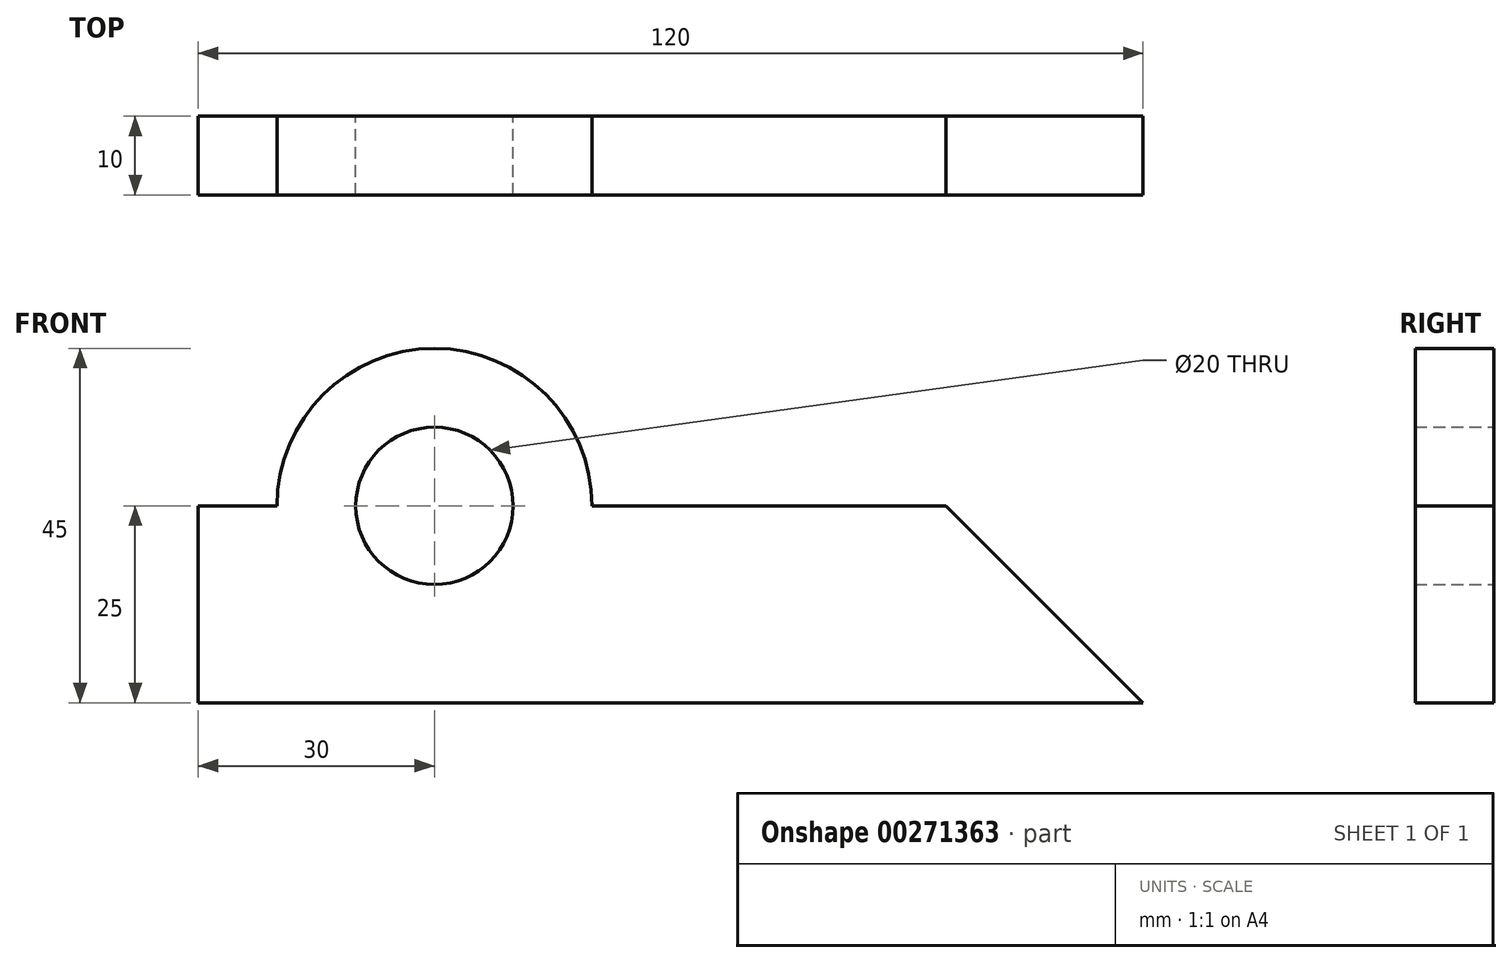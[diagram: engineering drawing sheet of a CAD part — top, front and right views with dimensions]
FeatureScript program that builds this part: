
annotation { "Feature Type Name" : "Feature", "Feature Type Description" : "" }
export const myFeature = defineFeature(function(context is Context, id is Id, definition is map)
    precondition{}
    {
        {
            var Q0;
            Q0=qCreatedBy(makeId("Front.planeOp"),FACE);
            var sketch = newSketch(context, id + "F0", { "sketchPlane" : qUnion([Q0])});
            skLineSegment(sketch, "E0.bottom", {"start": v(0, 0) * mm, "end": v(120, 0) * mm});
            skLineSegment(sketch, "E0.top", {"start": v(0, 25) * mm, "end": v(10, 25) * mm});
            skLineSegment(sketch, "E0.left", {"start": v(0, 0) * mm, "end": v(0, 25) * mm});
            skLineSegment(sketch, "E1", {"start": v(120, 0) * mm, "end": v(95, 25) * mm});
            skCircle(sketch, "E2", {"center": v(30, 25) * mm, "radius": 10 * mm});
            skLineSegment(sketch, "E3.trimOffspring", {"start": v(50, 25) * mm, "end": v(95, 25) * mm});
            skArc(sketch, "E4", {"start": v(50, 25) * mm, "mid": v(30, 45) * mm, "end": v(10, 25) * mm});
            skSolve(sketch);
        }
        {
            var Q0;
            Q0 = qSketchRegion(id + "F0", true);
            extrude(context, id + "F1", {"entities" : qUnion([Q0]), "depth" : 10 * mm});
        }
    });
